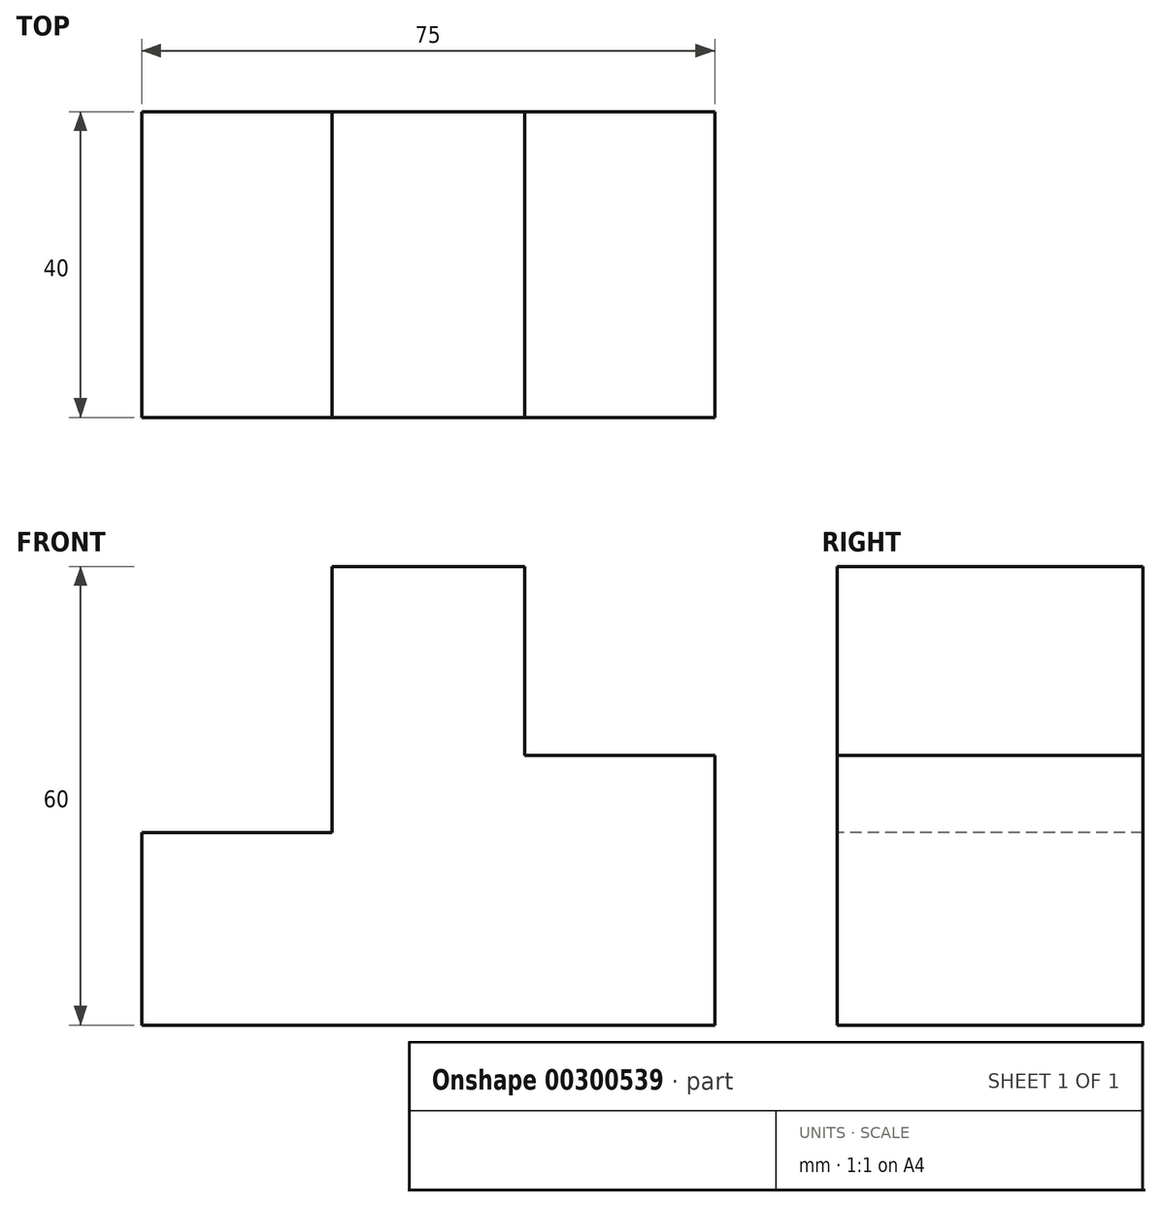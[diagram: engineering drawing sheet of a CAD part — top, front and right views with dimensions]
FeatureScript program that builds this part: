
annotation { "Feature Type Name" : "Feature", "Feature Type Description" : "" }
export const myFeature = defineFeature(function(context is Context, id is Id, definition is map)
    precondition{}
    {
        {
            var Q0;
            Q0=qCreatedBy(makeId("Front.planeOp"),FACE);
            var sketch = newSketch(context, id + "F0", { "sketchPlane" : qUnion([Q0])});
            skLineSegment(sketch, "E0.bottom", {"start": v(-31.63, 29.8) * mm, "end": v(43.37, 29.8) * mm});
            skLineSegment(sketch, "E0.top", {"start": v(-31.63, -30.2) * mm, "end": v(43.37, -30.2) * mm});
            skLineSegment(sketch, "E0.left", {"start": v(-31.63, 29.8) * mm, "end": v(-31.63, -30.2) * mm});
            skLineSegment(sketch, "E0.right", {"start": v(43.37, 29.8) * mm, "end": v(43.37, -30.2) * mm});
            skSolve(sketch);
        }
        {
            var Q0;
            Q0 = qSketchRegion(id + "F0", true);
            extrude(context, id + "F1", {"entities" : qUnion([Q0]), "depth" : 40 * mm});
        }
        {
            var Q0;
            Q0=qCreatedBy(makeId("Front.planeOp"),FACE);
            var sketch = newSketch(context, id + "F2", { "sketchPlane" : qUnion([Q0])});
            skLineSegment(sketch, "E1.bottom", {"start": v(-31.74, 29.98) * mm, "end": v(-6.74, 29.98) * mm});
            skLineSegment(sketch, "E1.top", {"start": v(-31.74, -5.02) * mm, "end": v(-6.74, -5.02) * mm});
            skLineSegment(sketch, "E1.left", {"start": v(-31.74, 29.98) * mm, "end": v(-31.74, -5.02) * mm});
            skLineSegment(sketch, "E1.right", {"start": v(-6.74, 29.98) * mm, "end": v(-6.74, -5.02) * mm});
            skLineSegment(sketch, "E2.bottom", {"start": v(43.48, 30.08) * mm, "end": v(18.49, 30.08) * mm});
            skLineSegment(sketch, "E2.top", {"start": v(43.48, 5.08) * mm, "end": v(18.49, 5.08) * mm});
            skLineSegment(sketch, "E2.left", {"start": v(43.48, 30.08) * mm, "end": v(43.48, 5.08) * mm});
            skLineSegment(sketch, "E2.right", {"start": v(18.49, 30.08) * mm, "end": v(18.49, 5.08) * mm});
            skSolve(sketch);
        }
        {
            var Q0;
            Q0 = qSketchRegion(id + "F2", true);
            extrude(context, id + "F3", {"entities" : qUnion([Q0]), "operationType" : NewBodyOperationType.REMOVE, "endBound" : BoundingType.THROUGH_ALL, "depth" : 25.4 * mm});
        }
    });
